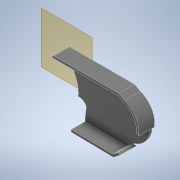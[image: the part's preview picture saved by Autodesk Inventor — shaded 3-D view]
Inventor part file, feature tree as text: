
AUTODESK INVENTOR PART (.ipt)
format: ipt  version: 2022 (Build 260153000, 153)  size: 348,672 bytes
history: native  units: in
note: dims shown in document units (in); Inventor stores cm internally (conversion verified against a paired STEP export)
features: plane x2, extrude x2, sketch x2, other x1
ambient origin geometry x8: Origin, YZ Plane, XZ Plane, XY Plane, X Axis, Y Axis, Z Axis, Center Point
bodies: Body1 (feature_tree)
feature tree (7):
  other  "Sólido1"
  plane  "Plano de trabajo2"
  extrude  "Extrusión2"  Depth=0.0394in
  plane  "Plano de trabajo1"
  extrude  "Extrusión3"  Depth=0.0394in
  sketch  "Boceto2"  dims[d8=0.0315in d9=0.0in d10=0.0394in d11=0.0394in d12=0.0394in]
  sketch  "Boceto3"  dims[d13=0.2677in d14=0.0in d15=0.0394in d16=0.0344in d17=0.0197in d18=0.0344in]
